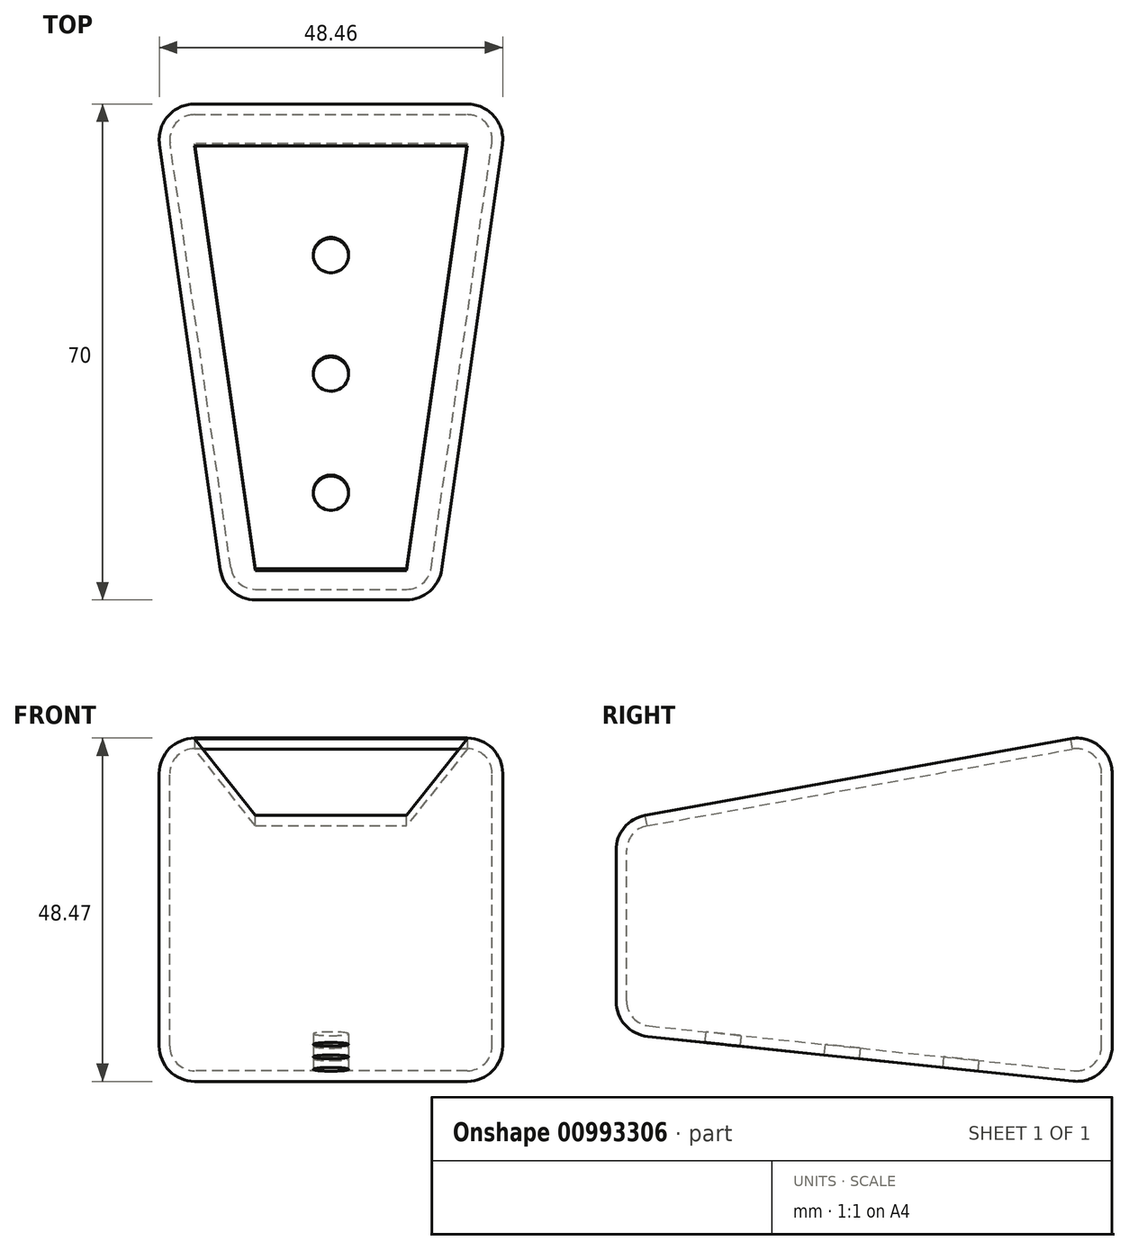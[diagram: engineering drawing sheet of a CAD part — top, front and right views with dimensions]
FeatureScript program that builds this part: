
annotation { "Feature Type Name" : "Feature", "Feature Type Description" : "" }
export const myFeature = defineFeature(function(context is Context, id is Id, definition is map)
    precondition{}
    {
        {
            var Q0;
            Q0=qCreatedBy(makeId("Front.planeOp"),FACE);
            var sketch = newSketch(context, id + "F0", { "sketchPlane" : qUnion([Q0])});
            skLineSegment(sketch, "E0.bottom", {"start": v(-25, 25) * mm, "end": v(25, 25) * mm});
            skLineSegment(sketch, "E0.top", {"start": v(-25, -25) * mm, "end": v(25, -25) * mm});
            skLineSegment(sketch, "E0.left", {"start": v(-25, 25) * mm, "end": v(-25, -25) * mm});
            skLineSegment(sketch, "E0.right", {"start": v(25, 25) * mm, "end": v(25, -25) * mm});
            skLineSegment(sketch, "E1", {"start": v(0, 0) * mm, "end": v(-25, 25) * mm, "construction": true});
            skLineSegment(sketch, "E2", {"start": v(0, 0) * mm, "end": v(25, 25) * mm, "construction": true});
            skLineSegment(sketch, "E3", {"start": v(0, 0) * mm, "end": v(-25, -25) * mm, "construction": true});
            skSolve(sketch);
        }
        {
            var Q0;
            Q0=makeQuery(id+"F0.imprint","IMPRINT",FACE,{"disambiguationData":[TD([[makeQuery(id+"F0.imprint","IMPRINT",EDGE,{"derivedFrom":sQuery(id+"F0.wireOp",EDGE,"E0.bottom")}),-1.0]])]});
            cPlane(context, id + "F1", {"entities" : qUnion([Q0]), "cplaneType" : CPlaneType.OFFSET, "offset" : 70 * mm, "width" : 150 * mm, "height" : 150 * mm});
        }
        {
            var Q0;
            Q0=qCreatedBy(id+"F1.planeOp",FACE);
            var sketch = newSketch(context, id + "F2", { "sketchPlane" : qUnion([Q0])});
            skLineSegment(sketch, "E4.bottom", {"start": v(-15, 12.36) * mm, "end": v(15, 12.36) * mm});
            skLineSegment(sketch, "E4.top", {"start": v(-15, -17.64) * mm, "end": v(15, -17.64) * mm});
            skLineSegment(sketch, "E4.left", {"start": v(-15, 12.36) * mm, "end": v(-15, -17.64) * mm});
            skLineSegment(sketch, "E4.right", {"start": v(15, 12.36) * mm, "end": v(15, -17.64) * mm});
            skLineSegment(sketch, "E5", {"start": v(0, 0) * mm, "end": v(-15, 12.36) * mm, "construction": true});
            skLineSegment(sketch, "E6", {"start": v(0, 0) * mm, "end": v(15, 12.36) * mm, "construction": true});
            skSolve(sketch);
        }
        {
            var Q0;
            Q0=makeQuery(id+"F0.imprint","IMPRINT",FACE,{"disambiguationData":[TD([[makeQuery(id+"F0.imprint","IMPRINT",EDGE,{"derivedFrom":sQuery(id+"F0.wireOp",EDGE,"E0.bottom")}),-1.0]])]});
            var Q1;
            Q1=makeQuery(id+"F2.imprint","IMPRINT",FACE,{"disambiguationData":[TD([[makeQuery(id+"F2.imprint","IMPRINT",EDGE,{"derivedFrom":sQuery(id+"F2.wireOp",EDGE,"E4.bottom")}),-1.0]])]});
            loft(context, id + "F3", {"sheetProfilesArray" : [{ "sheetProfileEntities" : qUnion([Q0]) }, { "sheetProfileEntities" : qUnion([Q1]) }]});
        }
        {
            var Q0;
            Q0=makeQuery(id+"F3.opLoft","MID_CAP_EDGE",EDGE,{"disambiguationData":[OSD([sQuery(id+"F2.wireOp",EDGE,"E4.bottom"),sQuery(id+"F2.wireOp",EDGE,"E4.left"),sQuery(id+"F2.wireOp",EDGE,"E4.right")])],"capPos":1.0});
            var Q1;
            Q1=makeQuery(id+"F3.opLoft","MID_CAP_EDGE",EDGE,{"disambiguationData":[OSD([sQuery(id+"F2.wireOp",EDGE,"E4.bottom"),sQuery(id+"F2.wireOp",EDGE,"E4.top"),sQuery(id+"F2.wireOp",EDGE,"E4.right")])],"capPos":1.0});
            var Q2;
            Q2=makeQuery(id+"F3.opLoft","MID_CAP_EDGE",EDGE,{"disambiguationData":[OSD([sQuery(id+"F2.wireOp",EDGE,"E4.bottom"),sQuery(id+"F2.wireOp",EDGE,"E4.top"),sQuery(id+"F2.wireOp",EDGE,"E4.left")])],"capPos":1.0});
            var Q3;
            Q3=makeQuery(id+"F3.opLoft","SWEPT_EDGE",EDGE,{"disambiguationData":[OSD([sQuery(id+"F0.wireOp",EDGE,"E0.top"),sQuery(id+"F0.wireOp",EDGE,"E0.right"),sQuery(id+"F2.wireOp",EDGE,"E4.top"),sQuery(id+"F2.wireOp",EDGE,"E4.right")])]});
            var Q4;
            Q4=makeQuery(id+"F3.opLoft","SWEPT_EDGE",EDGE,{"disambiguationData":[OSD([sQuery(id+"F0.wireOp",EDGE,"E0.top"),sQuery(id+"F0.wireOp",EDGE,"E0.left"),sQuery(id+"F2.wireOp",EDGE,"E4.top"),sQuery(id+"F2.wireOp",EDGE,"E4.left")])]});
            var Q5;
            Q5=makeQuery(id+"F3.opLoft","SWEPT_EDGE",EDGE,{"disambiguationData":[OSD([sQuery(id+"F0.wireOp",EDGE,"E0.bottom"),sQuery(id+"F0.wireOp",EDGE,"E0.left"),sQuery(id+"F2.wireOp",EDGE,"E4.bottom"),sQuery(id+"F2.wireOp",EDGE,"E4.left")])]});
            var Q6;
            Q6=makeQuery(id+"F3.opLoft","SWEPT_EDGE",EDGE,{"disambiguationData":[OSD([sQuery(id+"F0.wireOp",EDGE,"E0.bottom"),sQuery(id+"F0.wireOp",EDGE,"E0.right"),sQuery(id+"F2.wireOp",EDGE,"E4.bottom"),sQuery(id+"F2.wireOp",EDGE,"E4.right")])]});
            var Q7;
            Q7=makeQuery(id+"F3.opLoft","MID_CAP_EDGE",EDGE,{"disambiguationData":[OSD([sQuery(id+"F2.wireOp",EDGE,"E4.top"),sQuery(id+"F2.wireOp",EDGE,"E4.left"),sQuery(id+"F2.wireOp",EDGE,"E4.right")])],"capPos":1.0});
            var Q8;
            Q8=makeQuery(id+"F3.opLoft","MID_CAP_EDGE",EDGE,{"disambiguationData":[OSD([sQuery(id+"F0.wireOp",EDGE,"E0.bottom"),sQuery(id+"F0.wireOp",EDGE,"E0.left"),sQuery(id+"F0.wireOp",EDGE,"E0.right")])],"capPos":0.0});
            var Q9;
            Q9=makeQuery(id+"F3.opLoft","MID_CAP_EDGE",EDGE,{"disambiguationData":[OSD([sQuery(id+"F0.wireOp",EDGE,"E0.top"),sQuery(id+"F0.wireOp",EDGE,"E0.left"),sQuery(id+"F0.wireOp",EDGE,"E0.right")])],"capPos":0.0});
            var Q10;
            Q10=makeQuery(id+"F3.opLoft","MID_CAP_EDGE",EDGE,{"disambiguationData":[OSD([sQuery(id+"F0.wireOp",EDGE,"E0.bottom"),sQuery(id+"F0.wireOp",EDGE,"E0.top"),sQuery(id+"F0.wireOp",EDGE,"E0.left")])],"capPos":0.0});
            var Q11;
            Q11=makeQuery(id+"F3.opLoft","MID_CAP_EDGE",EDGE,{"disambiguationData":[OSD([sQuery(id+"F0.wireOp",EDGE,"E0.bottom"),sQuery(id+"F0.wireOp",EDGE,"E0.top"),sQuery(id+"F0.wireOp",EDGE,"E0.right")])],"capPos":0.0});
            fillet(context, id + "F4", {"entities" : qUnion([Q0, Q1, Q2, Q3, Q4, Q5, Q6, Q7, Q8, Q9, Q10, Q11]), "radius" : 5 * mm, "tangentPropagation" : true, "allowEdgeOverflow" : false});
        }
        {
            var Q0;
            Q0=makeQuery(id+"F3.opLoft","SWEPT_FACE",FACE,{"disambiguationData":[OSD([sQuery(id+"F0.wireOp",EDGE,"E0.bottom"),sQuery(id+"F0.wireOp",EDGE,"E0.left"),sQuery(id+"F0.wireOp",EDGE,"E0.right"),sQuery(id+"F2.wireOp",EDGE,"E4.bottom"),sQuery(id+"F2.wireOp",EDGE,"E4.left"),sQuery(id+"F2.wireOp",EDGE,"E4.right")])]});
            shell(context, id + "F5", {"entities" : qUnion([Q0]), "thickness" : 1.5 * mm});
        }
        {
            var Q0;
            Q0=makeQuery(id+"F3.opLoft","SWEPT_FACE",FACE,{"disambiguationData":[OSD([sQuery(id+"F0.wireOp",EDGE,"E0.top"),sQuery(id+"F0.wireOp",EDGE,"E0.left"),sQuery(id+"F0.wireOp",EDGE,"E0.right"),sQuery(id+"F2.wireOp",EDGE,"E4.top"),sQuery(id+"F2.wireOp",EDGE,"E4.left"),sQuery(id+"F2.wireOp",EDGE,"E4.right")])]});
            var sketch = newSketch(context, id + "F6", { "sketchPlane" : qUnion([Q0])});
            skCircle(sketch, "E7", {"center": v(0, 18.98) * mm, "radius": 2.5 * mm});
            skCircle(sketch, "E8", {"center": v(0, 35.8) * mm, "radius": 2.5 * mm});
            skCircle(sketch, "E9", {"center": v(0, 52.7) * mm, "radius": 2.5 * mm});
            skSolve(sketch);
        }
        {
            var Q0;
            Q0=makeQuery(id+"F6.imprint","IMPRINT",FACE,{"disambiguationData":[TD([[makeQuery(id+"F6.imprint","IMPRINT",EDGE,{"derivedFrom":sQuery(id+"F6.wireOp",EDGE,"E8")}),1.0]])]});
            var Q1;
            Q1=makeQuery(id+"F6.imprint","IMPRINT",FACE,{"disambiguationData":[TD([[makeQuery(id+"F6.imprint","IMPRINT",EDGE,{"derivedFrom":sQuery(id+"F6.wireOp",EDGE,"E9")}),1.0]])]});
            var Q2;
            Q2=makeQuery(id+"F6.imprint","IMPRINT",FACE,{"disambiguationData":[TD([[makeQuery(id+"F6.imprint","IMPRINT",EDGE,{"derivedFrom":sQuery(id+"F6.wireOp",EDGE,"E7")}),1.0]])]});
            extrude(context, id + "F7", {"entities" : qUnion([Q0, Q1, Q2]), "operationType" : NewBodyOperationType.REMOVE, "endBound" : BoundingType.THROUGH_ALL, "oppositeDirection" : true, "depth" : 25 * mm, "offsetDistance" : 25 * mm});
        }
    });
